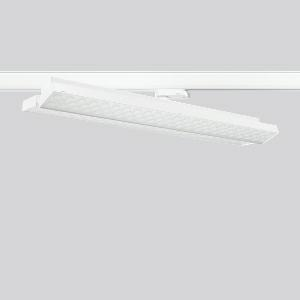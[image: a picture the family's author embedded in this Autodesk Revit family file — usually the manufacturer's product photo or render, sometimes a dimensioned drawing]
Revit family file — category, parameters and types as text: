
# Revit family: tx-move_742163_002_76_b92d
name_source: partatom
category: Lighting Fixtures
units: mm (PartAtom-declared; Revit-internal decimal feet)

## family parameters
Cut with Voids When Loaded = No
Host = Face
Light Source = No
Part Type = Normal
Room Calculation Point = No
Round Connector Dimension = Use Diameter
Shared = No

## types (1)
- MultiLumen 1 (1 x LED Modul 830, 2750 lm, 3000)
    Apparent Load = 41 VA
    CIE Flux Codes = 65 90 98 100 100
    Color Rendering = 80
    Color Temperature = 3000
    Default Elevation = 1800 mm
    Description = Series: TX-MOVE
Multifunctional surface-mounted spotlight for area lighting. Very flat design. Housing: sheet steel, powder-coated. Rotation range: 356°. Swivel range: 90°. Consistent alignment possible with visible tilt scale. High-efficiency LED units with optimum light control thanks to clear plastic (PC) lens optics. Spezielle Mikrostrukturen reduzieren Gelbsaum. Asymmetrical light distribution. With adapter for RZB 3-circuit DALI tracks. Suitable for Track on ceiling. MultiLumen: Luminous flux adjustable in 3 steps. Factory setting is the highest luminous flux. Environmentally friendly and resource-saving due to replaceable and recyclable components. 
Colour: traffic white, matt (RAL 9016)
Length: 570 mm
Width: 119 mm
Height: 88 mm
Lamp: LED
Socket: without socket
Colour temperature: 3000K
Colour rendering index (CRI): 80
System power: 41 W
Rated luminous flux: 5500 lm
Luminous efficiency: 134 lm/W
System power 2: 57 W
Rated luminous flux 2: 7400 lm
Luminous efficiency 2: 130 lm/W
System power 3: 73 W
Rated luminous flux 3: 9050 lm
Luminous efficiency 3: 124 lm/W
Control gear: Dimmable EVG, DALI
Protection class: I
Type of protection: IP 20
    Height = 75 mm
    Lamp = 1 x LED Modul 830
    Lamp Light Flux = 2750 lm
    Lamp count = 1
    Length = 569 mm
    Lifetime = 50000 h
    Luminous efficacy = 134 lm/W
    Manufacturer = RZB
    ModVariant = No
    Model = 742163.002.76
    Mounting Place = Ceiling
    Mounting Type = Surface mounted
    Number of Poles = 1
    OnlyDefault = Yes
    Power Factor = 1
    Product Name = TX-MOVE
    Product group = Track mounted projectors
    ProductGroupID = 301
    Protection Class = Protection class I
    Protection Degree = IP 20
    RLX_Detail_Level = 1
    RLX_Emergency_Light_Flux = 0 lm
    RLX_Emergency_Type = 0
    RLX_Emergency_Type_DB = No
    RlxData = <blob elided: 52069 chars, md5=2dfa0408>
    Socket = socket
    Standby Power = 0 W
    System Light Flux = 5500 lm
    System Power = 41 W
    Type Comments = MultiLumen 1
    Type Image = 742162.002.jpg
    URL = http://relux.com
    VarID = multilumen_1
    Voltage = 0 V
    Weight = 0.00 kg
    Width = 119 mm

## geometry (parser evidence)
native form markers: Blend x4, Sweep x13
no freeform markers — native parametric forms only
